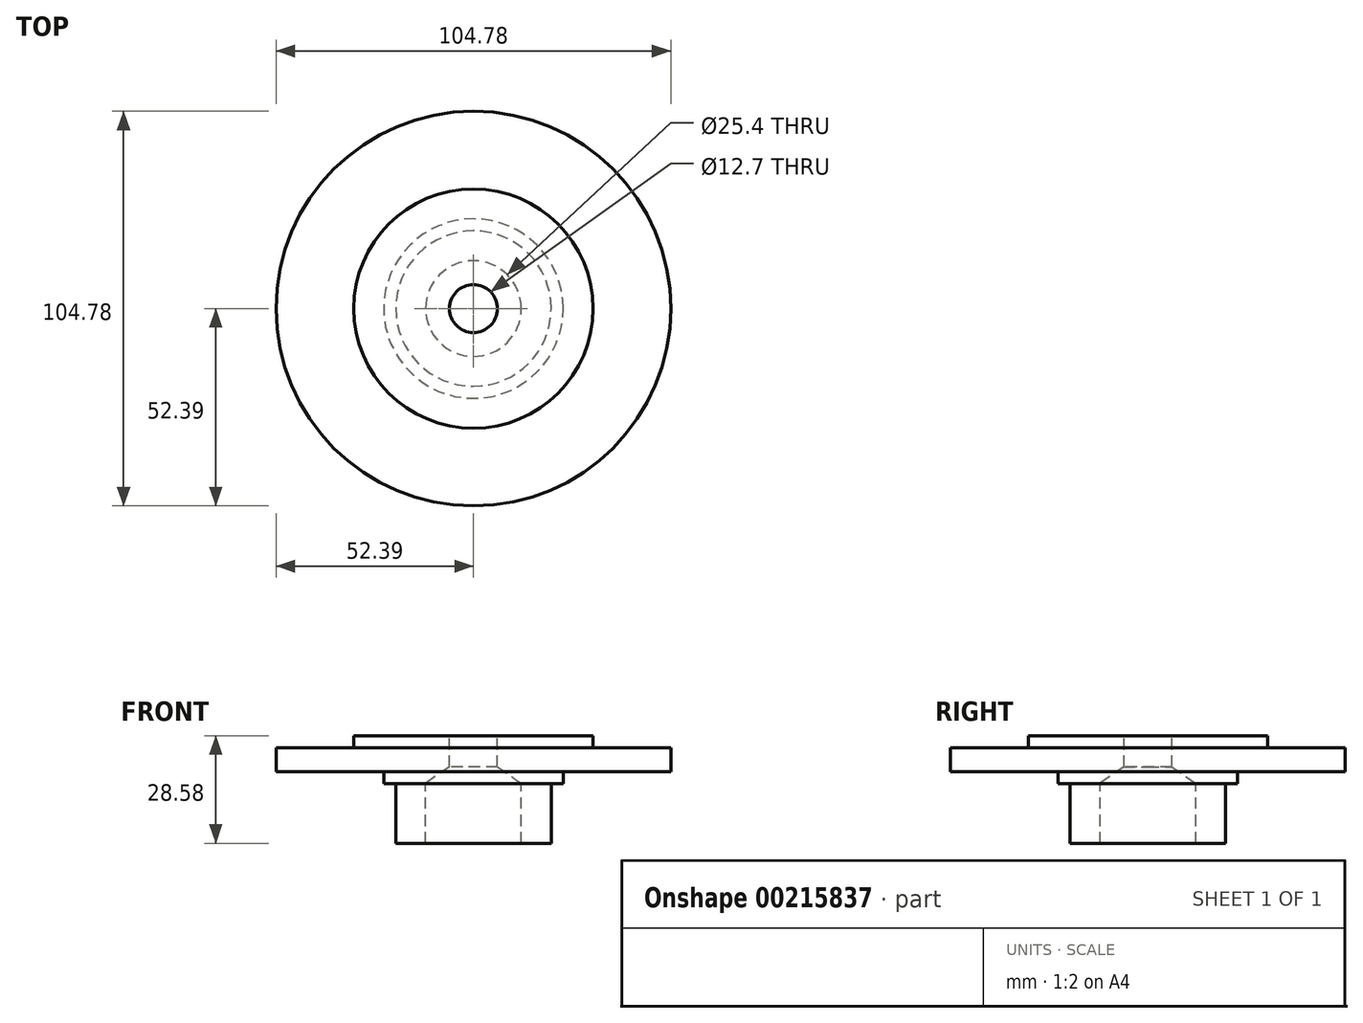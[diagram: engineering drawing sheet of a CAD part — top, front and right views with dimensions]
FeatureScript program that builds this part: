
annotation { "Feature Type Name" : "Feature", "Feature Type Description" : "" }
export const myFeature = defineFeature(function(context is Context, id is Id, definition is map)
    precondition{}
    {
        {
            var Q0;
            Q0=qCreatedBy(makeId("Front.planeOp"),FACE);
            var sketch = newSketch(context, id + "F0", { "sketchPlane" : qUnion([Q0])});
            skLineSegment(sketch, "E0", {"start": v(-31.75, 3.18) * mm, "end": v(-31.75, 0) * mm});
            skLineSegment(sketch, "E1", {"start": v(-31.75, 0) * mm, "end": v(-52.39, 0) * mm});
            skLineSegment(sketch, "E2", {"start": v(-52.39, 0) * mm, "end": v(-52.39, -6.35) * mm});
            skLineSegment(sketch, "E3", {"start": v(-52.39, -6.35) * mm, "end": v(-23.81, -6.35) * mm});
            skLineSegment(sketch, "E4", {"start": v(-23.81, -6.35) * mm, "end": v(-23.81, -9.53) * mm});
            skLineSegment(sketch, "E5", {"start": v(-23.81, -9.52) * mm, "end": v(-20.64, -9.52) * mm});
            skLineSegment(sketch, "E6", {"start": v(-20.64, -9.53) * mm, "end": v(-20.64, -25.4) * mm});
            skLineSegment(sketch, "E7", {"start": v(-20.64, -25.4) * mm, "end": v(-12.7, -25.4) * mm});
            skLineSegment(sketch, "E8", {"start": v(-12.7, -25.4) * mm, "end": v(-12.7, -9.53) * mm});
            skLineSegment(sketch, "E9", {"start": v(-12.7, -9.53) * mm, "end": v(-6.35, -5.08) * mm});
            skLineSegment(sketch, "E10", {"start": v(-6.35, -5.08) * mm, "end": v(-6.35, 3.18) * mm});
            skLineSegment(sketch, "E11", {"start": v(-6.35, 3.18) * mm, "end": v(-31.75, 3.18) * mm});
            skLineSegment(sketch, "E12", {"start": v(0, 29.56) * mm, "end": v(0, -37.88) * mm, "construction": true});
            skSolve(sketch);
        }
        {
            var Q0;
            Q0=qSketchRegion(id+"F0",true);
            var Q1;
            Q1=sQuery(id+"F0.wireOp",EDGE,"E12");
            revolve(context, id + "F1", {"entities" : qUnion([Q0]), "axis" : qUnion([Q1]), "revolveType" : RevolveType.FULL});
        }
    });
